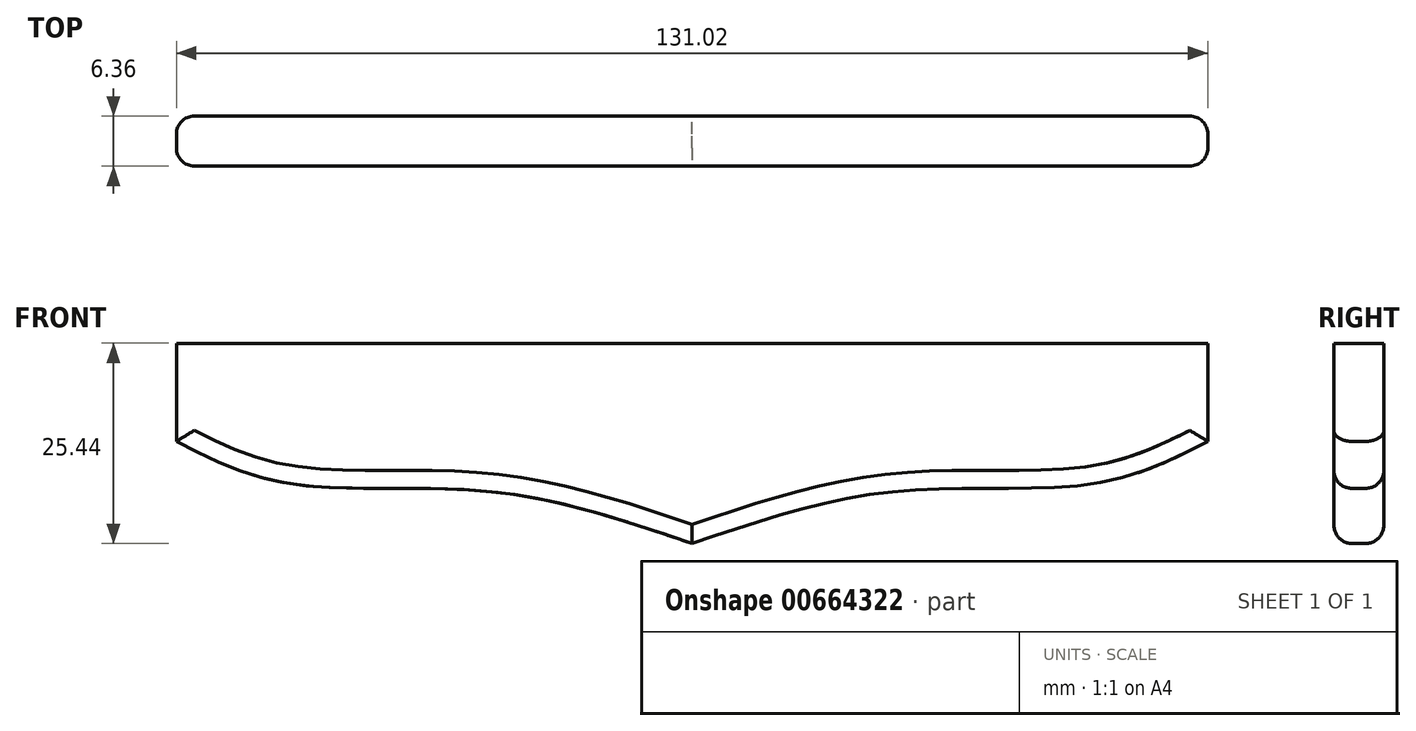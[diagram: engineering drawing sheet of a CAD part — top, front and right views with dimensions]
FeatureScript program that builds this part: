
annotation { "Feature Type Name" : "Feature", "Feature Type Description" : "" }
export const myFeature = defineFeature(function(context is Context, id is Id, definition is map)
    precondition{}
    {
        {
            var Q0;
            Q0=qCreatedBy(makeId("Front.planeOp"),FACE);
            var sketch = newSketch(context, id + "F0", { "sketchPlane" : qUnion([Q0])});
            skLineSegment(sketch, "E0.bottom", {"start": v(0, 0) * mm, "end": v(-65.5, 0) * mm});
            skLineSegment(sketch, "E0.top", {"start": v(0, 12.47) * mm, "end": v(-65.5, 12.47) * mm});
            skLineSegment(sketch, "E0.left", {"start": v(0, 0) * mm, "end": v(0, 12.47) * mm});
            skLineSegment(sketch, "E0.right", {"start": v(-65.5, 0) * mm, "end": v(-65.5, 12.47) * mm});
            skLineSegment(sketch, "E1", {"start": v(0, 0) * mm, "end": v(0, -12.97) * mm});
            skFitSpline(sketch, "E2", {"points": [v(0, -12.97) * mm, v(-25.82, -6.36) * mm, v(-51.26, -5.34) * mm, v(-65.5, 0) * mm], "startDerivative": vector(-68.9, 23.48) * mm, "endDerivative": vector(-46.9, 24.07) * mm});
            skLineSegment(sketch, "E3.MirrorCS", {"start": v(0, 0) * mm, "end": v(65.5, 0) * mm});
            skLineSegment(sketch, "E4.MirrorCS", {"start": v(65.5, 0) * mm, "end": v(65.5, 12.47) * mm});
            skLineSegment(sketch, "E5.MirrorCS", {"start": v(0, 12.47) * mm, "end": v(65.5, 12.47) * mm});
            skFitSpline(sketch, "E6.MirrorCS", {"points": [v(0, -12.97) * mm, v(25.82, -6.36) * mm, v(51.26, -5.34) * mm, v(65.5, 0) * mm], "startDerivative": vector(68.9, 23.48) * mm, "endDerivative": vector(46.9, 24.07) * mm});
            skSolve(sketch);
        }
        {
            var Q0;
            Q0=makeQuery(id+"F0.imprint","IMPRINT",FACE,{"disambiguationData":[TD([[makeQuery(id+"F0.imprint","IMPRINT",EDGE,{"derivedFrom":sQuery(id+"F0.wireOp",EDGE,"E0.left")}),-1.0]])]});
            var Q1;
            Q1=makeQuery(id+"F0.imprint","IMPRINT",FACE,{"disambiguationData":[TD([[makeQuery(id+"F0.imprint","IMPRINT",EDGE,{"derivedFrom":sQuery(id+"F0.wireOp",EDGE,"E0.bottom")}),-1.0]])]});
            var Q2;
            Q2=makeQuery(id+"F0.imprint","IMPRINT",FACE,{"disambiguationData":[TD([[makeQuery(id+"F0.imprint","IMPRINT",EDGE,{"derivedFrom":sQuery(id+"F0.wireOp",EDGE,"E1")}),1.0]])]});
            var Q3;
            Q3=makeQuery(id+"F0.imprint","IMPRINT",FACE,{"disambiguationData":[TD([[makeQuery(id+"F0.imprint","IMPRINT",EDGE,{"derivedFrom":sQuery(id+"F0.wireOp",EDGE,"E0.bottom")}),1.0]])]});
            extrude(context, id + "F1", {"entities" : qUnion([Q0, Q1, Q2, Q3]), "endBound" : BoundingType.SYMMETRIC, "depth" : 6.35 * mm, "offsetDistance" : 25.4 * mm});
        }
        {
            var Q0;
            Q0=makeQuery(id+"F1.opExtrude","CAP_EDGE",EDGE,{"disambiguationData":[OSD([sQuery(id+"F0.wireOp",EDGE,"E2")])],"isStart":false});
            var Q1;
            Q1=makeQuery(id+"F1.opExtrude","CAP_EDGE",EDGE,{"disambiguationData":[OSD([sQuery(id+"F0.wireOp",EDGE,"E6.MirrorCS")])],"isStart":false});
            var Q2;
            Q2=makeQuery(id+"F1.opExtrude","CAP_EDGE",EDGE,{"disambiguationData":[OSD([sQuery(id+"F0.wireOp",EDGE,"E6.MirrorCS")])],"isStart":true});
            var Q3;
            Q3=makeQuery(id+"F1.opExtrude","CAP_EDGE",EDGE,{"disambiguationData":[OSD([sQuery(id+"F0.wireOp",EDGE,"E2")])],"isStart":true});
            var Q4;
            Q4=makeQuery(id+"F1.opExtrude","CAP_EDGE",EDGE,{"disambiguationData":[OSD([sQuery(id+"F0.wireOp",EDGE,"E4.MirrorCS")])],"isStart":true});
            var Q5;
            Q5=makeQuery(id+"F1.opExtrude","CAP_EDGE",EDGE,{"disambiguationData":[OSD([sQuery(id+"F0.wireOp",EDGE,"E4.MirrorCS")])],"isStart":false});
            var Q6;
            Q6=makeQuery(id+"F1.opExtrude","CAP_EDGE",EDGE,{"disambiguationData":[OSD([sQuery(id+"F0.wireOp",EDGE,"E0.right")])],"isStart":true});
            var Q7;
            Q7=makeQuery(id+"F1.opExtrude","CAP_EDGE",EDGE,{"disambiguationData":[OSD([sQuery(id+"F0.wireOp",EDGE,"E0.right")])],"isStart":false});
            fillet(context, id + "F2", {"entities" : qUnion([Q0, Q1, Q2, Q3, Q4, Q5, Q6, Q7]), "radius" : 2.3 * mm, "tangentPropagation" : true, "allowEdgeOverflow" : false});
        }
    });
